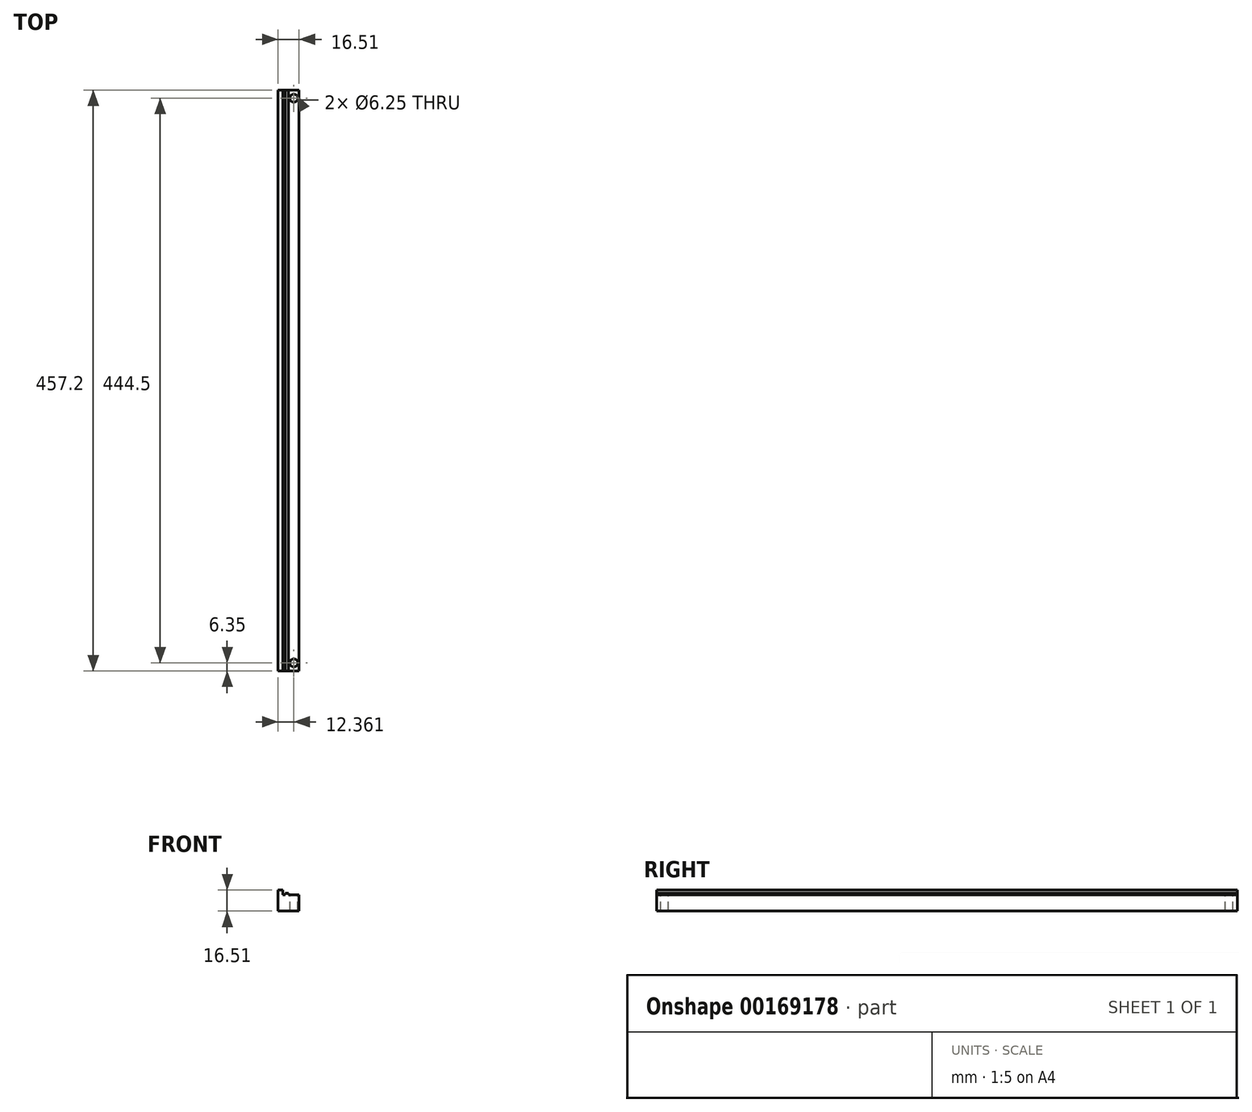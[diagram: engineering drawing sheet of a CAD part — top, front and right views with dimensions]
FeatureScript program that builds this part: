
annotation { "Feature Type Name" : "Feature", "Feature Type Description" : "" }
export const myFeature = defineFeature(function(context is Context, id is Id, definition is map)
    precondition{}
    {
        {
            var Q0;
            Q0=qCreatedBy(makeId("Front.planeOp"),FACE);
            var sketch = newSketch(context, id + "F0", { "sketchPlane" : qUnion([Q0])});
            skLineSegment(sketch, "E0", {"start": v(0, 0) * mm, "end": v(16.51, 0) * mm});
            skLineSegment(sketch, "E1", {"start": v(16.51, 0) * mm, "end": v(16.51, 12.7) * mm});
            skLineSegment(sketch, "E2", {"start": v(16.51, 12.7) * mm, "end": v(8.21, 12.7) * mm});
            skLineSegment(sketch, "E3", {"start": v(8.21, 12.7) * mm, "end": v(8.21, 14.1) * mm});
            skLineSegment(sketch, "E4", {"start": v(8.21, 14.1) * mm, "end": v(5.41, 14.1) * mm});
            skLineSegment(sketch, "E5", {"start": v(5.41, 14.1) * mm, "end": v(5.41, 12.7) * mm});
            skLineSegment(sketch, "E6", {"start": v(5.41, 12.7) * mm, "end": v(0, 12.7) * mm});
            skLineSegment(sketch, "E7", {"start": v(0, 12.7) * mm, "end": v(0, 0) * mm});
            skLineSegment(sketch, "E8", {"start": v(0, 12.7) * mm, "end": v(0, 16.51) * mm});
            skLineSegment(sketch, "E9", {"start": v(0, 16.51) * mm, "end": v(3.81, 16.51) * mm});
            skLineSegment(sketch, "E10", {"start": v(3.8, 16.51) * mm, "end": v(3.81, 12.7) * mm});
            skSolve(sketch);
        }
        {
            var Q0;
            Q0=makeQuery(id+"F0.imprint","IMPRINT",FACE,{"disambiguationData":[TD([[makeQuery(id+"F0.imprint","IMPRINT",EDGE,{"derivedFrom":sQuery(id+"F0.wireOp",EDGE,"E0")}),1.0]])]});
            var Q1;
            {var subQ0=sQuery(id+"F0.wireOp",EDGE,"E8");Q1=makeQuery(id+"F0.imprint","IMPRINT",FACE,{"disambiguationData":[TD([[makeQuery(id+"F0.imprint","IMPRINT",EDGE,{"derivedFrom":subQ0}),-1.0]])]});}
            extrude(context, id + "F1", {"entities" : qUnion([Q0, Q1]), "depth" : 457.2 * mm});
        }
        {
            var Q0;
            Q0=makeQuery(id+"F1.opExtrude","SWEPT_FACE",FACE,{"disambiguationData":[OSD([sQuery(id+"F0.wireOp",EDGE,"E2")])]});
            var sketch = newSketch(context, id + "F2", { "sketchPlane" : qUnion([Q0])});
            skPoint(sketch, "E11", {"position": v(12.36, -450.85) * mm});
            skPoint(sketch, "E12", {"position": v(12.36, -6.35) * mm});
            skSolve(sketch);
        }
        {
            var Q0;
            Q0=sQuery(id+"F2.wireOp",VERTEX,"E12");
            var Q1;
            Q1=sQuery(id+"F2.wireOp",VERTEX,"E11");
            var Q2;
            Q2=makeQuery(id+"F1.opExtrude","SWEPT_BODY",BODY,{"disambiguationData":[OSD([sQuery(id+"F0.wireOp",EDGE,"E0"),sQuery(id+"F0.wireOp",EDGE,"E1"),sQuery(id+"F0.wireOp",EDGE,"E2"),sQuery(id+"F0.wireOp",EDGE,"E3"),sQuery(id+"F0.wireOp",EDGE,"E4"),sQuery(id+"F0.wireOp",EDGE,"E5"),sQuery(id+"F0.wireOp",EDGE,"E6"),sQuery(id+"F0.wireOp",EDGE,"E7"),sQuery(id+"F0.wireOp",EDGE,"E8"),sQuery(id+"F0.wireOp",EDGE,"E9"),sQuery(id+"F0.wireOp",EDGE,"E10")])]});
            hole(context, id + "F3", {"style" : HoleStyle.SIMPLE, "endStyle" : HoleEndStyle.THROUGH, "standardTappedOrClearance" : lookupTablePath({ "standard" : "ANSI", "size" : "D (0.25)", "type" : "Drilled" }), "standardBlindInLast" : lookupTablePath({ "standard" : "ANSI", "size" : "D", "type" : "Drilled" }), "holeDiameter" : 6.25 * mm, "startFromSketch" : true, "locations" : qUnion([Q0, Q1]), "scope" : qUnion([Q2]), "isTappedThrough" : true});
        }
    });
